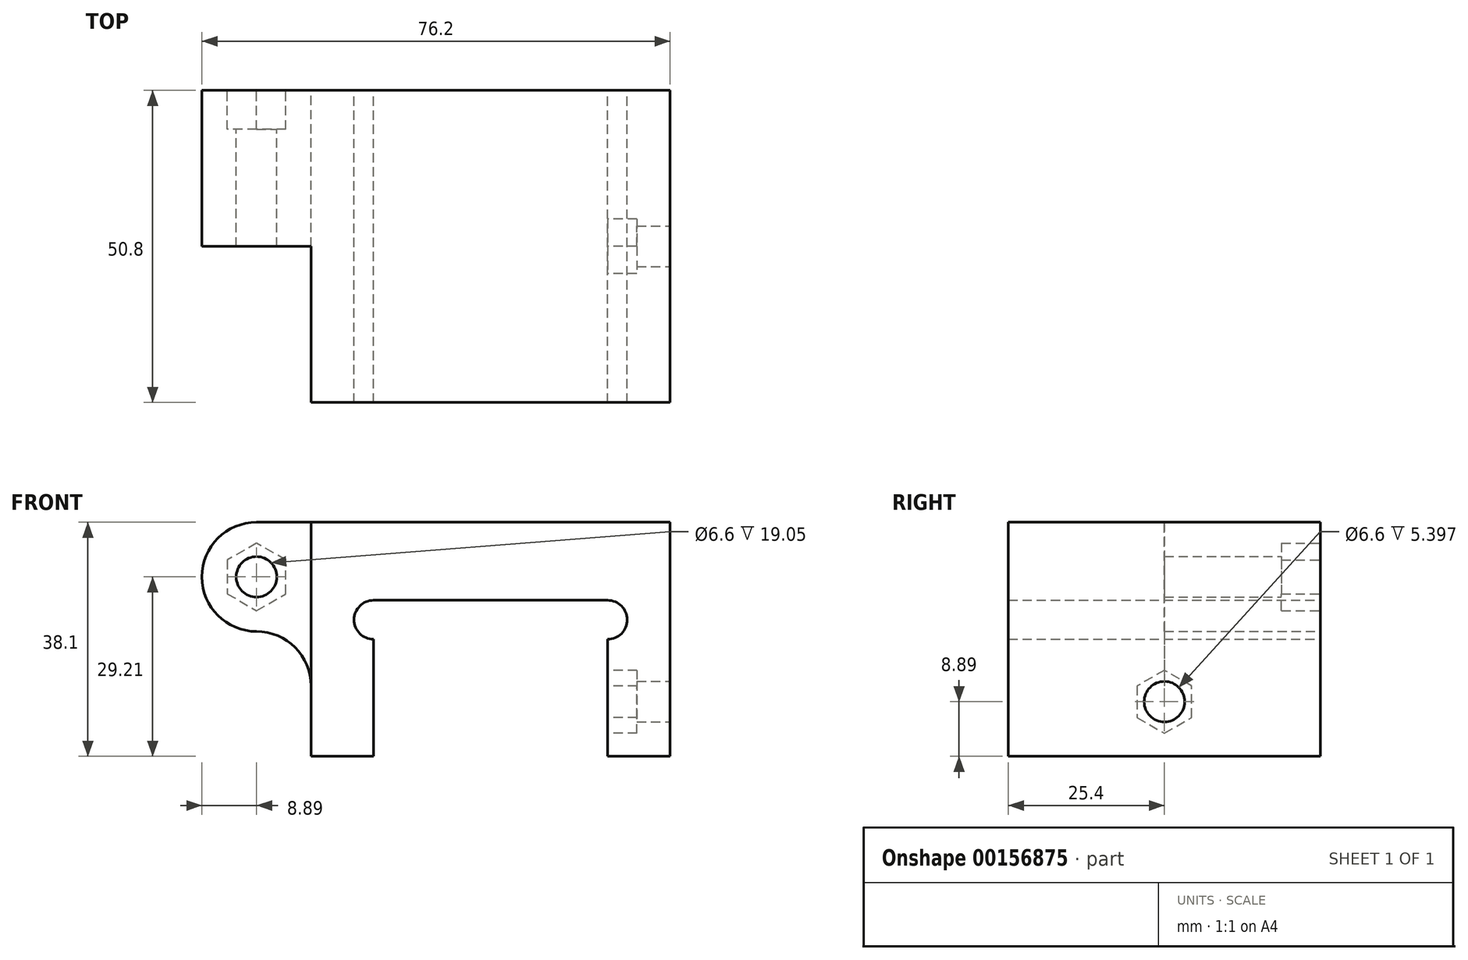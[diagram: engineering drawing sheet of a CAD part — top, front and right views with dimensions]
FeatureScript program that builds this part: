
annotation { "Feature Type Name" : "Feature", "Feature Type Description" : "" }
export const myFeature = defineFeature(function(context is Context, id is Id, definition is map)
    precondition{}
    {
        {
            var Q0;
            Q0=qCreatedBy(makeId("Front.planeOp"),FACE);
            var sketch = newSketch(context, id + "F0", { "sketchPlane" : qUnion([Q0])});
            skLineSegment(sketch, "E0.bottom", {"start": v(0, 0) * mm, "end": v(10.16, 0) * mm});
            skLineSegment(sketch, "E0.top", {"start": v(-8.89, 38.1) * mm, "end": v(58.42, 38.1) * mm});
            skLineSegment(sketch, "E0.right", {"start": v(58.42, 0) * mm, "end": v(58.42, 38.1) * mm});
            skLineSegment(sketch, "E1.top", {"start": v(10.16, 25.4) * mm, "end": v(48.26, 25.4) * mm});
            skLineSegment(sketch, "E1.left", {"start": v(48.26, 0) * mm, "end": v(48.26, 19.05) * mm});
            skLineSegment(sketch, "E1.right", {"start": v(10.16, 0) * mm, "end": v(10.16, 19.05) * mm});
            skArc(sketch, "E2", {"start": v(48.26, 19.05) * mm, "mid": v(51.44, 22.22) * mm, "end": v(48.26, 25.4) * mm});
            skArc(sketch, "E3", {"start": v(10.16, 25.4) * mm, "mid": v(6.99, 22.22) * mm, "end": v(10.16, 19.05) * mm});
            skArc(sketch, "E4", {"start": v(-8.9, 38.1) * mm, "mid": v(-17.78, 29.2) * mm, "end": v(-8.9, 20.32) * mm});
            skCircle(sketch, "E5", {"center": v(-8.9, 29.2) * mm, "radius": 3.3 * mm});
            skLineSegment(sketch, "E6", {"start": v(0, 11.43) * mm, "end": v(0, 0) * mm});
            skArc(sketch, "E7", {"start": v(0, 11.43) * mm, "mid": v(-2.6, 17.72) * mm, "end": v(-8.9, 20.32) * mm});
            skLineSegment(sketch, "E8.trimOffspring", {"start": v(48.26, 0) * mm, "end": v(58.42, 0) * mm});
            skSolve(sketch);
        }
        {
            var Q0;
            Q0=makeQuery(id+"F0.imprint","IMPRINT",FACE,{"disambiguationData":[TD([[makeQuery(id+"F0.imprint","IMPRINT",EDGE,{"derivedFrom":sQuery(id+"F0.wireOp",EDGE,"E0.bottom")}),1.0]])]});
            extrude(context, id + "F1", {"entities" : qUnion([Q0]), "depth" : 50.8 * mm});
        }
        {
            var Q0;
            Q0=makeQuery(id+"F1.opExtrude","SWEPT_FACE",FACE,{"disambiguationData":[OSD([sQuery(id+"F0.wireOp",EDGE,"E0.bottom")])]});
            var sketch = newSketch(context, id + "F2", { "sketchPlane" : qUnion([Q0])});
            skLineSegment(sketch, "E9.0", {"start": v(-8.9, 50.8) * mm, "end": v(-17.78, 50.8) * mm});
            skLineSegment(sketch, "E10.0", {"start": v(0, 50.8) * mm, "end": v(-8.9, 50.8) * mm});
            skLineSegment(sketch, "E11.0", {"start": v(0, 50.8) * mm, "end": v(0, 0) * mm});
            skPoint(sketch, "E12", {"position": v(0, 25.4) * mm});
            skLineSegment(sketch, "E13.bottom", {"start": v(-17.78, 50.8) * mm, "end": v(0, 50.8) * mm});
            skLineSegment(sketch, "E13.top", {"start": v(-17.78, 25.4) * mm, "end": v(0, 25.4) * mm});
            skLineSegment(sketch, "E13.left", {"start": v(-17.78, 50.8) * mm, "end": v(-17.78, 25.4) * mm});
            skLineSegment(sketch, "E13.right", {"start": v(0, 50.8) * mm, "end": v(0, 25.4) * mm});
            skSolve(sketch);
        }
        {
            var Q0;
            Q0=makeQuery(id+"F2.imprint","IMPRINT",FACE,{"disambiguationData":[TD([[makeQuery(id+"F2.imprint","IMPRINT",EDGE,{"derivedFrom":sQuery(id+"F2.wireOp",EDGE,"E13.top")}),1.0]])]});
            extrude(context, id + "F3", {"entities" : qUnion([Q0]), "operationType" : NewBodyOperationType.REMOVE, "endBound" : BoundingType.THROUGH_ALL, "oppositeDirection" : true, "depth" : 25.4 * mm});
        }
        {
            var Q0;
            Q0=makeQuery(id+"F1.opExtrude","CAP_FACE",FACE,{"disambiguationData":[OSD([sQuery(id+"F0.wireOp",EDGE,"E0.bottom"),sQuery(id+"F0.wireOp",EDGE,"E0.top"),sQuery(id+"F0.wireOp",EDGE,"E0.right"),sQuery(id+"F0.wireOp",EDGE,"E1.top"),sQuery(id+"F0.wireOp",EDGE,"E1.left"),sQuery(id+"F0.wireOp",EDGE,"E1.right"),sQuery(id+"F0.wireOp",EDGE,"E2"),sQuery(id+"F0.wireOp",EDGE,"E3"),sQuery(id+"F0.wireOp",EDGE,"E4"),sQuery(id+"F0.wireOp",EDGE,"E5"),sQuery(id+"F0.wireOp",EDGE,"E6"),sQuery(id+"F0.wireOp",EDGE,"E7"),sQuery(id+"F0.wireOp",EDGE,"E8.trimOffspring")])],"isStart":true});
            var sketch = newSketch(context, id + "F4", { "sketchPlane" : qUnion([Q0])});
            skCircle(sketch, "E14.cCircle", {"center": v(8.9, 29.2) * mm, "radius": 5.5 * mm, "construction": true});
            skLineSegment(sketch, "E14.0", {"start": v(13.65, 31.96) * mm, "end": v(13.65, 26.46) * mm});
            skLineSegment(sketch, "E14.1", {"start": v(13.65, 26.46) * mm, "end": v(8.9, 23.71) * mm});
            skLineSegment(sketch, "E14.2", {"start": v(8.9, 23.71) * mm, "end": v(4.13, 26.46) * mm});
            skLineSegment(sketch, "E14.3", {"start": v(4.13, 26.46) * mm, "end": v(4.13, 31.96) * mm});
            skLineSegment(sketch, "E14.4", {"start": v(4.13, 31.96) * mm, "end": v(8.9, 34.7) * mm});
            skLineSegment(sketch, "E14.5", {"start": v(8.9, 34.7) * mm, "end": v(13.65, 31.96) * mm});
            skSolve(sketch);
        }
        {
            var Q0;
            Q0=makeQuery(id+"F4.imprint","IMPRINT",FACE,{"disambiguationData":[TD([[makeQuery(id+"F4.imprint","IMPRINT",EDGE,{"derivedFrom":sQuery(id+"F4.wireOp",EDGE,"E14.0")}),-1.0]])]});
            extrude(context, id + "F5", {"entities" : qUnion([Q0]), "operationType" : NewBodyOperationType.REMOVE, "oppositeDirection" : true, "depth" : 6.35 * mm});
        }
        {
            var Q0;
            Q0=makeQuery(id+"F1.opExtrude","SWEPT_FACE",FACE,{"disambiguationData":[OSD([sQuery(id+"F0.wireOp",EDGE,"E0.right")])]});
            var sketch = newSketch(context, id + "F6", { "sketchPlane" : qUnion([Q0])});
            skPoint(sketch, "E15", {"position": v(-25.4, 0) * mm});
            skCircle(sketch, "E16", {"center": v(-25.4, 8.89) * mm, "radius": 3.3 * mm});
            skSolve(sketch);
        }
        {
            var Q0;
            Q0=makeQuery(id+"F6.imprint","IMPRINT",FACE,{"disambiguationData":[TD([[makeQuery(id+"F6.imprint","IMPRINT",EDGE,{"derivedFrom":sQuery(id+"F6.wireOp",EDGE,"E16")}),1.0]])]});
            extrude(context, id + "F7", {"entities" : qUnion([Q0]), "operationType" : NewBodyOperationType.REMOVE, "endBound" : BoundingType.UP_TO_NEXT, "oppositeDirection" : true, "depth" : 25.4 * mm});
        }
        {
            var Q0;
            Q0=makeQuery(id+"F1.opExtrude","SWEPT_FACE",FACE,{"disambiguationData":[OSD([sQuery(id+"F0.wireOp",EDGE,"E1.left")])]});
            var sketch = newSketch(context, id + "F8", { "sketchPlane" : qUnion([Q0])});
            skCircle(sketch, "E17.cCircle", {"center": v(25.4, 8.89) * mm, "radius": 5.13 * mm, "construction": true});
            skLineSegment(sketch, "E17.0", {"start": v(25.4, 14.02) * mm, "end": v(29.85, 11.46) * mm});
            skLineSegment(sketch, "E17.1", {"start": v(29.85, 11.46) * mm, "end": v(29.85, 6.32) * mm});
            skLineSegment(sketch, "E17.2", {"start": v(29.85, 6.32) * mm, "end": v(25.4, 3.76) * mm});
            skLineSegment(sketch, "E17.3", {"start": v(25.4, 3.76) * mm, "end": v(20.96, 6.32) * mm});
            skLineSegment(sketch, "E17.4", {"start": v(20.96, 6.32) * mm, "end": v(20.96, 11.46) * mm});
            skLineSegment(sketch, "E17.5", {"start": v(20.96, 11.46) * mm, "end": v(25.4, 14.02) * mm});
            skSolve(sketch);
        }
        {
            var Q0;
            Q0=makeQuery(id+"F8.imprint","IMPRINT",FACE,{"disambiguationData":[TD([[makeQuery(id+"F8.imprint","IMPRINT",EDGE,{"derivedFrom":sQuery(id+"F8.wireOp",EDGE,"E17.0")}),-1.0]])]});
            extrude(context, id + "F9", {"entities" : qUnion([Q0]), "operationType" : NewBodyOperationType.REMOVE, "oppositeDirection" : true, "depth" : 4.76 * mm});
        }
    });
